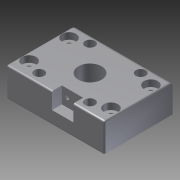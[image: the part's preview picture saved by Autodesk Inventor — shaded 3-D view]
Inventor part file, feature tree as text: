
AUTODESK INVENTOR PART (.ipt)
format: ipt  version: 2012 (Build 160160000, 160)  size: 207,360 bytes
history: native  units: mm
features: extrude x5, sketch x5, fillet x2
ambient origin geometry x8: Origin, YZ Plane, XZ Plane, XY Plane, X Axis, Y Axis, Z Axis, Center Point
bodies: Solid1 (feature_tree)
feature tree (12):
  extrude  "Extrusion1"  Depth=60.0mm
  fillet  "Fillet1"  Radius=10.0mm
  fillet  "Fillet2"  Radius=4.2mm
  extrude  "Extrusion2"  Depth=50.0mm
  extrude  "Extrusion3"  Depth=5.0mm
  extrude  "Extrusion4"  Depth=31.0mm
  extrude  "Extrusion5"  Depth=5.7mm
  sketch  "Sketch1"  dims[d0=42.4mm d1=60.0mm d2=10.0mm d3=4.2mm]
  sketch  "Sketch2"  dims[d4=24.4mm d5=50.0mm]
  sketch  "Sketch3"  dims[d6=9.0mm d7=5.0mm]
  sketch  "Sketch4"  dims[d8=6.0mm d9=31.0mm]
  sketch  "Sketch5"  dims[d10=31.0mm d11=5.7mm d12=14.5mm d13=30.0mm d14=21.2mm d15=18.0mm d16=0.0mm d17=1.0mm d18=3.0mm d19=8.5mm d20=4.0mm d21=0.0mm d22=19.0mm d23=13.0mm d24=10.0mm d25=6.0mm d26=0.0mm d27=2.1mm d28=5.0mm d29=6.5mm d30=3.25mm d31=14.0mm d32=0.0mm d33=14.2mm d34=15.5mm d35=0.0mm]
